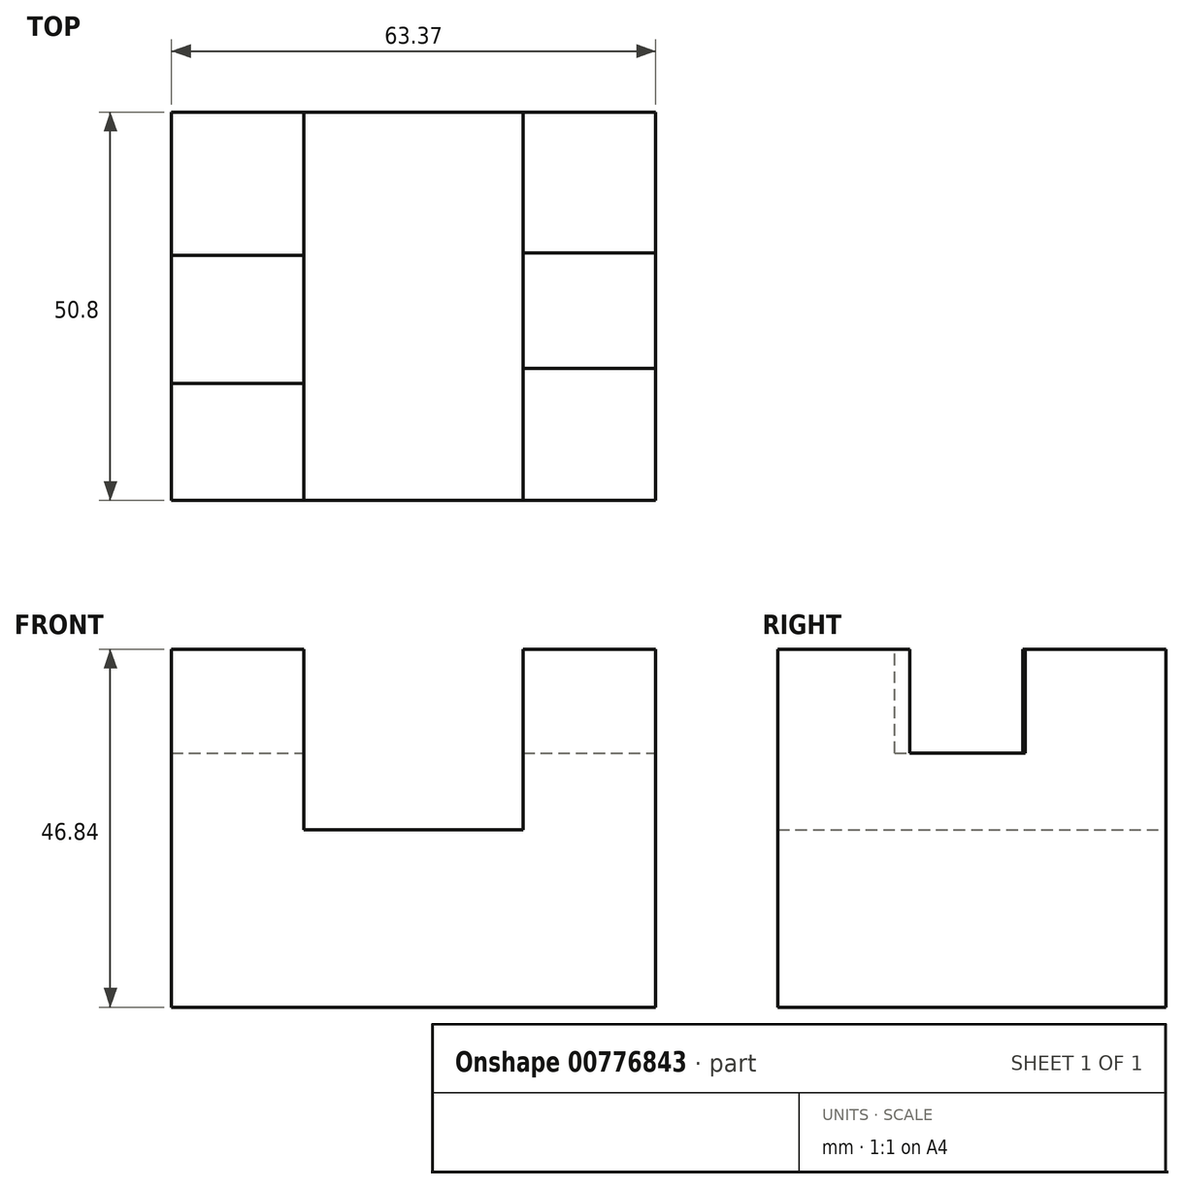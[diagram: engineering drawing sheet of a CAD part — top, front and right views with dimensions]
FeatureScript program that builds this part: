
annotation { "Feature Type Name" : "Feature", "Feature Type Description" : "" }
export const myFeature = defineFeature(function(context is Context, id is Id, definition is map)
    precondition{}
    {
        {
            var Q0;
            Q0=qCreatedBy(makeId("Front.planeOp"),FACE);
            var sketch = newSketch(context, id + "F0", { "sketchPlane" : qUnion([Q0])});
            skLineSegment(sketch, "E0.bottom", {"start": v(0, 0) * mm, "end": v(63.37, 0) * mm});
            skLineSegment(sketch, "E0.top", {"start": v(0, 46.84) * mm, "end": v(17.33, 46.84) * mm});
            skLineSegment(sketch, "E0.left", {"start": v(0, 0) * mm, "end": v(0, 46.84) * mm});
            skLineSegment(sketch, "E0.right", {"start": v(63.37, 0) * mm, "end": v(63.37, 46.84) * mm});
            skLineSegment(sketch, "E1.top", {"start": v(17.33, 23.19) * mm, "end": v(46.03, 23.19) * mm});
            skLineSegment(sketch, "E1.left", {"start": v(17.33, 46.84) * mm, "end": v(17.33, 23.19) * mm});
            skLineSegment(sketch, "E1.right", {"start": v(46.03, 46.84) * mm, "end": v(46.03, 23.19) * mm});
            skLineSegment(sketch, "E2.trimOffspring", {"start": v(46.03, 46.84) * mm, "end": v(63.37, 46.84) * mm});
            skSolve(sketch);
        }
        {
            var Q0;
            Q0=makeQuery(id+"F0.imprint","IMPRINT",FACE,{"disambiguationData":[TD([[makeQuery(id+"F0.imprint","IMPRINT",EDGE,{"derivedFrom":sQuery(id+"F0.wireOp",EDGE,"E0.bottom")}),1.0]])]});
            extrude(context, id + "F1", {"entities" : qUnion([Q0]), "depth" : 50.8 * mm, "offsetDistance" : 25.4 * mm});
        }
        {
            var Q0;
            Q0=makeQuery(id+"F1.opExtrude","SWEPT_FACE",FACE,{"disambiguationData":[OSD([sQuery(id+"F0.wireOp",EDGE,"E2.trimOffspring")])]});
            var sketch = newSketch(context, id + "F2", { "sketchPlane" : qUnion([Q0])});
            skLineSegment(sketch, "E3.bottom", {"start": v(46.03, -33.53) * mm, "end": v(63.37, -33.53) * mm});
            skLineSegment(sketch, "E3.top", {"start": v(46.03, -18.45) * mm, "end": v(63.37, -18.45) * mm});
            skLineSegment(sketch, "E3.left", {"start": v(46.03, -33.53) * mm, "end": v(46.03, -18.45) * mm});
            skLineSegment(sketch, "E3.right", {"start": v(63.37, -33.53) * mm, "end": v(63.37, -18.45) * mm});
            skSolve(sketch);
        }
        {
            var Q0;
            Q0=makeQuery(id+"F2.imprint","IMPRINT",FACE,{"disambiguationData":[TD([[makeQuery(id+"F2.imprint","IMPRINT",EDGE,{"derivedFrom":sQuery(id+"F2.wireOp",EDGE,"E3.bottom")}),1.0]])]});
            extrude(context, id + "F3", {"entities" : qUnion([Q0]), "operationType" : NewBodyOperationType.REMOVE, "oppositeDirection" : true, "depth" : 13.6 * mm, "offsetDistance" : 25.4 * mm});
        }
        {
            var Q0;
            Q0=makeQuery(id+"F1.opExtrude","SWEPT_FACE",FACE,{"disambiguationData":[OSD([sQuery(id+"F0.wireOp",EDGE,"E0.top")])]});
            var sketch = newSketch(context, id + "F4", { "sketchPlane" : qUnion([Q0])});
            skLineSegment(sketch, "E4.bottom", {"start": v(0, -35.5) * mm, "end": v(17.33, -35.5) * mm});
            skLineSegment(sketch, "E4.top", {"start": v(0, -18.74) * mm, "end": v(17.33, -18.74) * mm});
            skLineSegment(sketch, "E4.left", {"start": v(0, -35.5) * mm, "end": v(0, -18.74) * mm});
            skLineSegment(sketch, "E4.right", {"start": v(17.33, -35.5) * mm, "end": v(17.33, -18.74) * mm});
            skSolve(sketch);
        }
        {
            var Q0;
            Q0=makeQuery(id+"F4.imprint","IMPRINT",FACE,{"disambiguationData":[TD([[makeQuery(id+"F4.imprint","IMPRINT",EDGE,{"derivedFrom":sQuery(id+"F4.wireOp",EDGE,"E4.bottom")}),1.0]])]});
            extrude(context, id + "F5", {"entities" : qUnion([Q0]), "operationType" : NewBodyOperationType.REMOVE, "oppositeDirection" : true, "depth" : 13.6 * mm, "offsetDistance" : 25.4 * mm});
        }
    });
